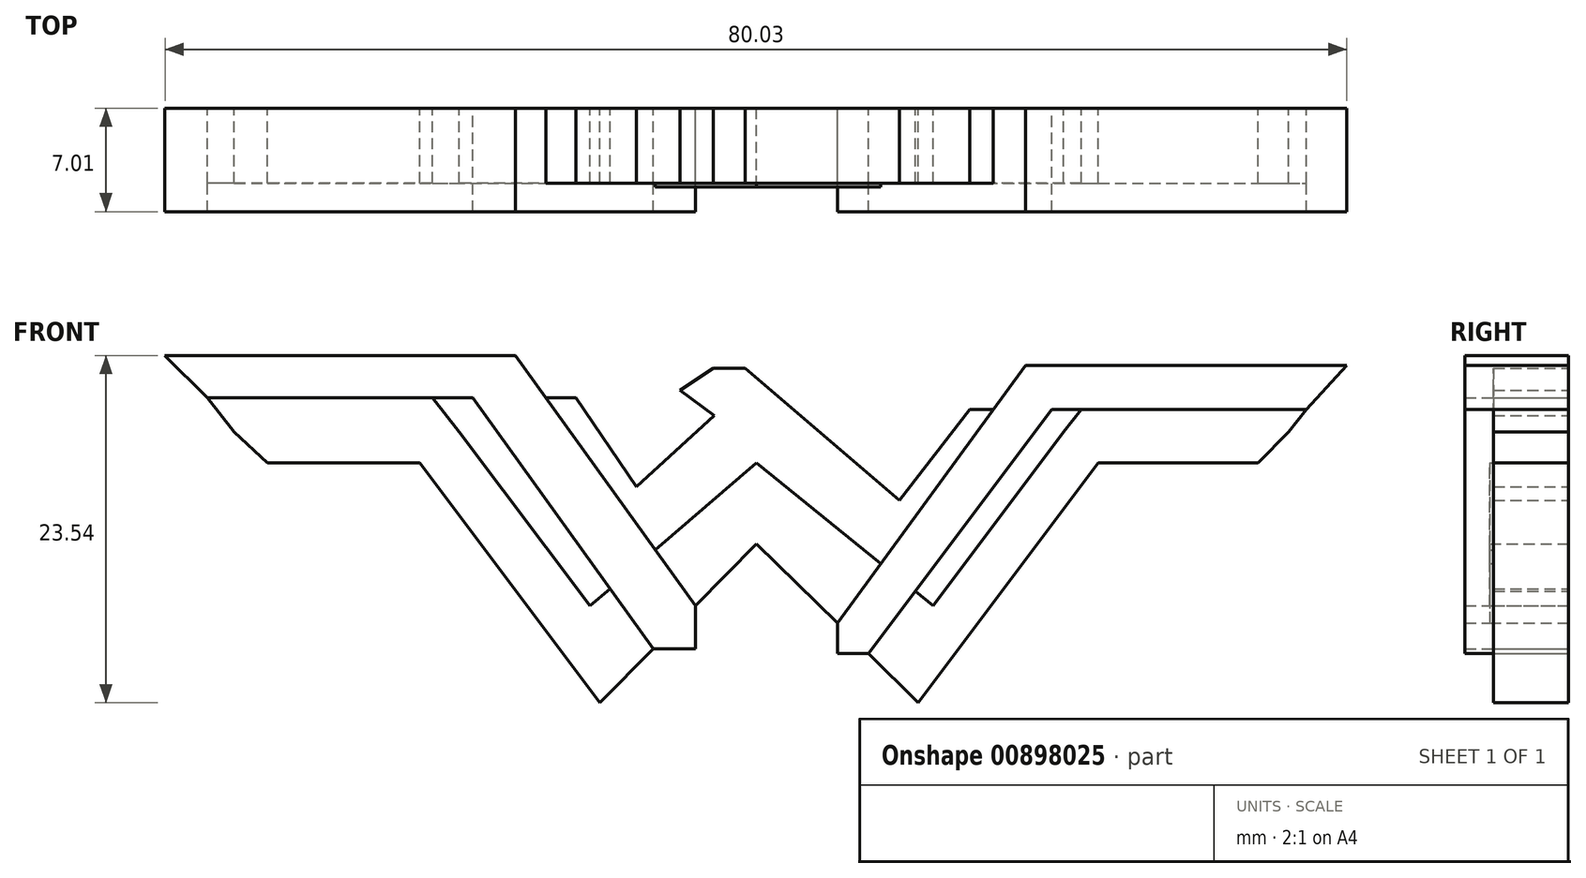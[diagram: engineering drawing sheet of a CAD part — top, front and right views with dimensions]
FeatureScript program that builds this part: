
annotation { "Feature Type Name" : "Feature", "Feature Type Description" : "" }
export const myFeature = defineFeature(function(context is Context, id is Id, definition is map)
    precondition{}
    {
        {
            var Q0;
            Q0=qCreatedBy(makeId("Front.planeOp"),FACE);
            var sketch = newSketch(context, id + "F0", { "sketchPlane" : qUnion([Q0])});
            skLineSegment(sketch, "E0", {"start": v(-33.12, 0) * mm, "end": v(-22.81, 0) * mm});
            skLineSegment(sketch, "E1", {"start": v(-22.81, 0) * mm, "end": v(-10.6, -16.25) * mm});
            skLineSegment(sketch, "E2", {"start": v(-10.6, -16.25) * mm, "end": v(-7, -12.6) * mm});
            skLineSegment(sketch, "E3", {"start": v(0, -5.47) * mm, "end": v(5.47, -10.86) * mm});
            skLineSegment(sketch, "E4", {"start": v(10.95, -16.25) * mm, "end": v(23.15, 0) * mm});
            skLineSegment(sketch, "E5", {"start": v(23.15, 0) * mm, "end": v(33.98, 0) * mm});
            skLineSegment(sketch, "E6", {"start": v(33.98, 0) * mm, "end": v(36.04, 2.1) * mm});
            skLineSegment(sketch, "E7", {"start": v(36.04, 2.1) * mm, "end": v(20.8, 2.1) * mm});
            skLineSegment(sketch, "E8", {"start": v(20.8, 2.1) * mm, "end": v(11.95, -9.68) * mm});
            skLineSegment(sketch, "E9", {"start": v(11.95, -9.68) * mm, "end": v(10.74, -8.7) * mm});
            skLineSegment(sketch, "E10", {"start": v(0, 0) * mm, "end": v(-6.86, -5.9) * mm});
            skLineSegment(sketch, "E11", {"start": v(-11.28, -9.68) * mm, "end": v(-20.12, 2.1) * mm});
            skLineSegment(sketch, "E12", {"start": v(-20.12, 2.1) * mm, "end": v(-35.36, 2.1) * mm});
            skLineSegment(sketch, "E13", {"start": v(-35.36, 2.1) * mm, "end": v(-33.12, 0) * mm});
            skLineSegment(sketch, "E14", {"start": v(-35.36, 2.1) * mm, "end": v(-37.18, 4.42) * mm});
            skLineSegment(sketch, "E15", {"start": v(-37.18, 4.42) * mm, "end": v(-21.96, 4.42) * mm});
            skLineSegment(sketch, "E16", {"start": v(-21.96, 4.42) * mm, "end": v(-20.12, 2.1) * mm});
            skLineSegment(sketch, "E17", {"start": v(-21.96, 4.42) * mm, "end": v(-19.21, 4.42) * mm});
            skLineSegment(sketch, "E18", {"start": v(-12.23, 4.42) * mm, "end": v(-8.15, -1.61) * mm});
            skLineSegment(sketch, "E19", {"start": v(9.67, -2.53) * mm, "end": v(10.87, -3.46) * mm});
            skLineSegment(sketch, "E20", {"start": v(36.04, 2.1) * mm, "end": v(37.22, 3.62) * mm});
            skLineSegment(sketch, "E21", {"start": v(37.22, 3.62) * mm, "end": v(22, 3.62) * mm});
            skLineSegment(sketch, "E22", {"start": v(22, 3.62) * mm, "end": v(20.8, 2.1) * mm});
            skLineSegment(sketch, "E23", {"start": v(22, 3.62) * mm, "end": v(20, 3.62) * mm});
            skLineSegment(sketch, "E24", {"start": v(14.43, 3.62) * mm, "end": v(9.67, -2.53) * mm});
            skLineSegment(sketch, "E25", {"start": v(-2.88, 3.21) * mm, "end": v(-5.2, 4.92) * mm});
            skLineSegment(sketch, "E26", {"start": v(-5.2, 4.92) * mm, "end": v(-2.94, 6.44) * mm});
            skLineSegment(sketch, "E27", {"start": v(-2.94, 6.44) * mm, "end": v(-0.78, 6.44) * mm});
            skLineSegment(sketch, "E28", {"start": v(-0.78, 6.44) * mm, "end": v(9.67, -2.53) * mm});
            skLineSegment(sketch, "E29", {"start": v(-37.18, 4.42) * mm, "end": v(-40.06, 7.29) * mm});
            skLineSegment(sketch, "E30", {"start": v(-40.06, 7.29) * mm, "end": v(-16.32, 7.29) * mm});
            skLineSegment(sketch, "E31", {"start": v(-16.32, 7.29) * mm, "end": v(-4.15, -9.68) * mm});
            skLineSegment(sketch, "E32", {"start": v(-7, -12.6) * mm, "end": v(-19.21, 4.42) * mm});
            skLineSegment(sketch, "E33.trimOffspring", {"start": v(-14.27, 4.42) * mm, "end": v(-12.23, 4.42) * mm});
            skLineSegment(sketch, "E34.trimOffspring", {"start": v(-9.93, -8.52) * mm, "end": v(-11.28, -9.68) * mm});
            skLineSegment(sketch, "E35.trimOffspring", {"start": v(-9.23, -2.6) * mm, "end": v(-2.88, 3.21) * mm});
            skLineSegment(sketch, "E36.trimOffspring", {"start": v(-4.15, -9.68) * mm, "end": v(0, -5.47) * mm});
            skLineSegment(sketch, "E37", {"start": v(-7, -12.6) * mm, "end": v(-4.15, -12.6) * mm});
            skLineSegment(sketch, "E38", {"start": v(-4.15, -12.6) * mm, "end": v(-4.15, -9.68) * mm});
            skPoint(sketch, "E39.start.orphan", {"position": v(-12.23, -8.4) * mm});
            skLineSegment(sketch, "E40", {"start": v(37.22, 3.62) * mm, "end": v(39.97, 6.62) * mm});
            skLineSegment(sketch, "E41", {"start": v(39.97, 6.62) * mm, "end": v(18.22, 6.62) * mm});
            skLineSegment(sketch, "E42", {"start": v(18.22, 6.62) * mm, "end": v(5.47, -10.86) * mm});
            skLineSegment(sketch, "E43", {"start": v(5.47, -10.86) * mm, "end": v(5.47, -12.92) * mm});
            skLineSegment(sketch, "E44", {"start": v(5.47, -12.92) * mm, "end": v(7.57, -12.92) * mm});
            skLineSegment(sketch, "E45", {"start": v(7.57, -12.92) * mm, "end": v(20, 3.62) * mm});
            skLineSegment(sketch, "E46.trimOffspring", {"start": v(16.03, 3.62) * mm, "end": v(14.43, 3.62) * mm});
            skLineSegment(sketch, "E47.trimOffspring", {"start": v(8.42, -6.82) * mm, "end": v(0, 0) * mm});
            skLineSegment(sketch, "E48.trimOffspring", {"start": v(7.57, -12.92) * mm, "end": v(10.95, -16.25) * mm});
            skSolve(sketch);
        }
        {
            var Q0;
            Q0=makeQuery(id+"F0.imprint","IMPRINT",FACE,{"disambiguationData":[TD([[makeQuery(id+"F0.imprint","IMPRINT",EDGE,{"derivedFrom":sQuery(id+"F0.wireOp",EDGE,"E15")}),1.0]])]});
            var Q1;
            Q1=makeQuery(id+"F0.imprint","IMPRINT",FACE,{"disambiguationData":[TD([[makeQuery(id+"F0.imprint","IMPRINT",EDGE,{"derivedFrom":sQuery(id+"F0.wireOp",EDGE,"E21")}),-1.0]])]});
            var Q2;
            Q2=makeQuery(id+"F0.imprint","IMPRINT",FACE,{"disambiguationData":[TD([[makeQuery(id+"F0.imprint","IMPRINT",EDGE,{"derivedFrom":sQuery(id+"F0.wireOp",EDGE,"E0")}),1.0]])]});
            var Q3;
            Q3=makeQuery(id+"F0.imprint","IMPRINT",FACE,{"disambiguationData":[TD([[makeQuery(id+"F0.imprint","IMPRINT",EDGE,{"derivedFrom":sQuery(id+"F0.wireOp",EDGE,"E12")}),-1.0]])]});
            var Q4;
            {var subQ0=sQuery(id+"F0.wireOp",EDGE,"E18");Q4=makeQuery(id+"F0.imprint","IMPRINT",FACE,{"disambiguationData":[TD([[makeQuery(id+"F0.imprint","IMPRINT",EDGE,{"derivedFrom":subQ0}),-1.0]])]});}
            var Q5;
            {var subQ4=sQuery(id+"F0.wireOp",EDGE,"E10");Q5=makeQuery(id+"F0.imprint","IMPRINT",FACE,{"disambiguationData":[TD([[makeQuery(id+"F0.imprint","IMPRINT",EDGE,{"derivedFrom":subQ4}),-1.0]])]});}
            var Q6;
            {var subQ3=sQuery(id+"F0.wireOp",EDGE,"E3");Q6=makeQuery(id+"F0.imprint","IMPRINT",FACE,{"disambiguationData":[TD([[makeQuery(id+"F0.imprint","IMPRINT",EDGE,{"derivedFrom":subQ3}),1.0]])]});}
            var Q7;
            Q7=makeQuery(id+"F0.imprint","IMPRINT",FACE,{"disambiguationData":[TD([[makeQuery(id+"F0.imprint","IMPRINT",EDGE,{"derivedFrom":sQuery(id+"F0.wireOp",EDGE,"E4")}),1.0]])]});
            var Q8;
            Q8=makeQuery(id+"F0.imprint","IMPRINT",FACE,{"disambiguationData":[TD([[makeQuery(id+"F0.imprint","IMPRINT",EDGE,{"derivedFrom":sQuery(id+"F0.wireOp",EDGE,"E7")}),-1.0]])]});
            var Q9;
            {var subQ0=sQuery(id+"F0.wireOp",EDGE,"E19");Q9=makeQuery(id+"F0.imprint","IMPRINT",FACE,{"disambiguationData":[TD([[makeQuery(id+"F0.imprint","IMPRINT",EDGE,{"derivedFrom":subQ0}),1.0]])]});}
            extrude(context, id + "F1", {"entities" : qUnion([Q0, Q1, Q2, Q3, Q4, Q5, Q6, Q7, Q8, Q9]), "depth" : 5.08 * mm, "offsetDistance" : 25.4 * mm});
        }
        {
            var Q0;
            Q0=makeQuery(id+"F0.imprint","IMPRINT",FACE,{"disambiguationData":[TD([[makeQuery(id+"F0.imprint","IMPRINT",EDGE,{"derivedFrom":sQuery(id+"F0.wireOp",EDGE,"E21")}),-1.0]])]});
            var Q1;
            Q1=makeQuery(id+"F0.imprint","IMPRINT",FACE,{"disambiguationData":[TD([[makeQuery(id+"F0.imprint","IMPRINT",EDGE,{"derivedFrom":sQuery(id+"F0.wireOp",EDGE,"E15")}),1.0]])]});
            extrude(context, id + "F2", {"entities" : qUnion([Q0, Q1]), "operationType" : NewBodyOperationType.ADD, "depth" : 7 * mm, "offsetDistance" : 25.4 * mm});
        }
        {
            var Q0;
            {var subQ3=sQuery(id+"F0.wireOp",EDGE,"E3");Q0=makeQuery(id+"F0.imprint","IMPRINT",FACE,{"disambiguationData":[TD([[makeQuery(id+"F0.imprint","IMPRINT",EDGE,{"derivedFrom":subQ3}),1.0]])]});}
            extrude(context, id + "F3", {"entities" : qUnion([Q0]), "operationType" : NewBodyOperationType.ADD, "depth" : 5.33 * mm, "offsetDistance" : 25.4 * mm});
        }
    });
